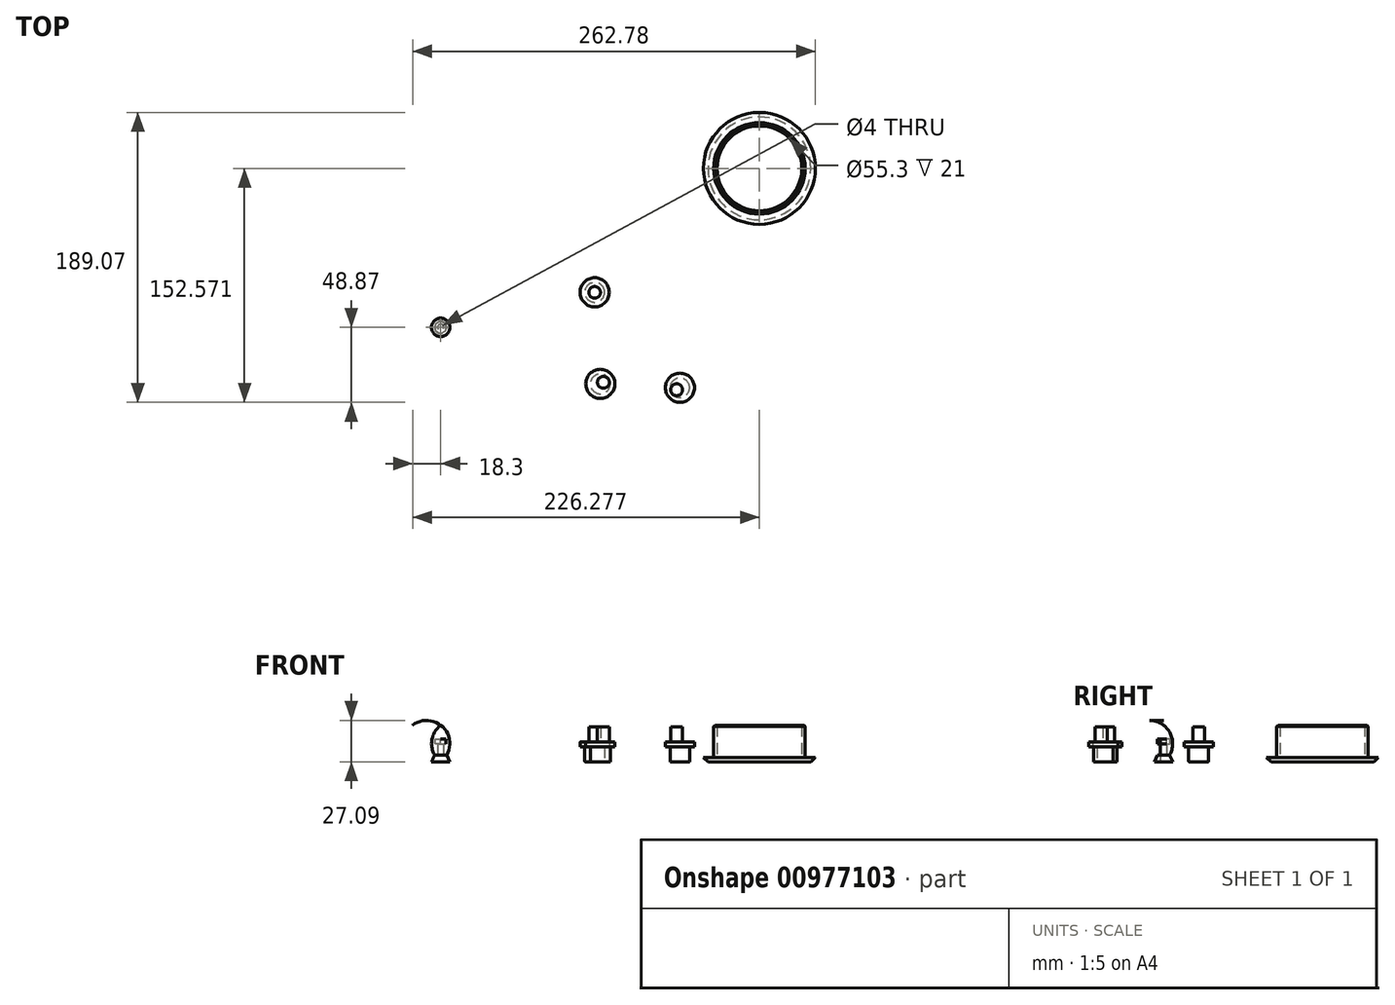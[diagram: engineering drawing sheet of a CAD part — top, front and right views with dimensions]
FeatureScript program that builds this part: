
annotation { "Feature Type Name" : "Feature", "Feature Type Description" : "" }
export const myFeature = defineFeature(function(context is Context, id is Id, definition is map)
    precondition{}
    {
        {
            var Q0;
            Q0=qCreatedBy(makeId("Front.planeOp"),FACE);
            var sketch = newSketch(context, id + "F0", { "sketchPlane" : qUnion([Q0])});
            skLineSegment(sketch, "E0.bottom", {"start": v(0, 0) * mm, "end": v(6, 0) * mm, "construction": true});
            skLineSegment(sketch, "E0.top", {"start": v(0, 24) * mm, "end": v(6, 24) * mm, "construction": true});
            skLineSegment(sketch, "E0.left", {"start": v(0, 0) * mm, "end": v(0, 24) * mm, "construction": true});
            skLineSegment(sketch, "E0.right", {"start": v(6, 0) * mm, "end": v(6, 24) * mm, "construction": true});
            skLineSegment(sketch, "E1", {"start": v(6, 4.5) * mm, "end": v(0, 4.5) * mm, "construction": true});
            skLineSegment(sketch, "E2", {"start": v(0, 24) * mm, "end": v(0, 28) * mm, "construction": true});
            skPoint(sketch, "E3", {"position": v(0.28, 24) * mm});
            skLineSegment(sketch, "E4", {"start": v(6, 14.25) * mm, "end": v(0, 14.25) * mm, "construction": true});
            skPoint(sketch, "E5", {"position": v(3, 24) * mm});
            skArc(sketch, "E6", {"start": v(3.94, 4.5) * mm, "mid": v(5.64, 15) * mm, "end": v(0, 24) * mm});
            skPoint(sketch, "E7", {"position": v(3.94, 4.5) * mm});
            skLineSegment(sketch, "E8", {"start": v(3.94, 4.5) * mm, "end": v(6, 0) * mm});
            skLineSegment(sketch, "E9", {"start": v(0, 0) * mm, "end": v(0, 24) * mm});
            skLineSegment(sketch, "E10", {"start": v(0, 0) * mm, "end": v(6, 0) * mm});
            skSolve(sketch);
        }
        {
            var Q0;
            Q0 = qSketchRegion(id + "F0", true);
            var Q1;
            Q1=sQuery(id+"F0.wireOp",EDGE,"E9");
            revolve(context, id + "F1", {"surfaceOperationType" : NewSurfaceOperationType.NEW, "entities" : qUnion([Q0]), "axis" : qUnion([Q1]), "revolveType" : RevolveType.FULL});
        }
        {
            var Q0;
            Q0=makeQuery(id+"F1.opRevolve","SWEPT_FACE",FACE,{"disambiguationData":[OSD([sQuery(id+"F0.wireOp",EDGE,"E10")])]});
            var sketch = newSketch(context, id + "F2", { "sketchPlane" : qUnion([Q0])});
            skCircle(sketch, "E11", {"center": v(0, 0) * mm, "radius": 2 * mm});
            skSolve(sketch);
        }
        {
            var Q0;
            Q0 = qSketchRegion(id + "F2", true);
            extrude(context, id + "F3", {"entities" : qUnion([Q0]), "operationType" : NewBodyOperationType.REMOVE, "oppositeDirection" : true, "depth" : 15 * mm, "offsetDistance" : 25 * mm});
        }
        {
            var Q0;
            Q0=makeQuery(id+"F3.boolean.opBoolean","COPY",FACE,{"derivedFrom":makeQuery(id+"F3.opExtrude","CAP_FACE",FACE,{"disambiguationData":[OSD([sQuery(id+"F2.wireOp",EDGE,"E11")])],"isStart":false})});
            var sketch = newSketch(context, id + "F4", { "sketchPlane" : qUnion([Q0])});
            skCircle(sketch, "E12.cCircle", {"center": v(0, 0) * mm, "radius": 4.1 * mm, "construction": true});
            skLineSegment(sketch, "E12.0", {"start": v(0, 4.1) * mm, "end": v(3.55, 2.05) * mm});
            skLineSegment(sketch, "E12.1", {"start": v(3.55, 2.05) * mm, "end": v(3.55, -2.05) * mm});
            skLineSegment(sketch, "E12.2", {"start": v(3.55, -2.05) * mm, "end": v(0, -4.1) * mm});
            skLineSegment(sketch, "E12.3", {"start": v(0, -4.1) * mm, "end": v(-3.55, -2.05) * mm});
            skLineSegment(sketch, "E12.4", {"start": v(-3.55, -2.05) * mm, "end": v(-3.55, 2.05) * mm});
            skLineSegment(sketch, "E12.5", {"start": v(-3.55, 2.05) * mm, "end": v(0, 4.1) * mm});
            skSolve(sketch);
        }
        {
            var Q0;
            Q0 = qSketchRegion(id + "F4", true);
            extrude(context, id + "F5", {"entities" : qUnion([Q0]), "operationType" : NewBodyOperationType.REMOVE, "depth" : 3.1 * mm, "offsetDistance" : 25 * mm});
        }
        {
            var Q0;
            Q0=qCreatedBy(makeId("Top.planeOp"),FACE);
            var sketch = newSketch(context, id + "F6", { "sketchPlane" : qUnion([Q0])});
            skCircle(sketch, "E13", {"center": v(100.5, 22.86) * mm, "radius": 6.45 * mm});
            skSolve(sketch);
        }
        {
            var Q0;
            Q0 = qSketchRegion(id + "F6", true);
            extrude(context, id + "F7", {"entities" : qUnion([Q0]), "depth" : 10 * mm, "offsetDistance" : 25 * mm});
        }
        {
            var Q0;
            Q0=makeQuery(id+"F7.opExtrude","CAP_FACE",FACE,{"disambiguationData":[OSD([sQuery(id+"F6.wireOp",EDGE,"E13")])],"isStart":false});
            var sketch = newSketch(context, id + "F8", { "sketchPlane" : qUnion([Q0])});
            skCircle(sketch, "E14", {"center": v(100.5, 22.86) * mm, "radius": 9.5 * mm});
            skSolve(sketch);
        }
        {
            var Q0;
            Q0=makeQuery(id+"F7.opExtrude","CAP_EDGE",EDGE,{"disambiguationData":[OSD([sQuery(id+"F6.wireOp",EDGE,"E13")])],"isStart":true});
            fillet(context, id + "F9", {"entities" : qUnion([Q0]), "tangentPropagation" : true, "radius" : 0.5 * mm, "defaultsChanged" : true, "vertexSettings" : [], "allowEdgeOverflow" : false});
        }
        {
            var Q0;
            Q0 = qSketchRegion(id + "F8", true);
            extrude(context, id + "F10", {"entities" : qUnion([Q0]), "operationType" : NewBodyOperationType.ADD, "depth" : 3 * mm, "offsetDistance" : 25 * mm});
        }
        {
            var Q0;
            Q0=makeQuery(id+"F10.opExtrude","CAP_FACE",FACE,{"disambiguationData":[OSD([sQuery(id+"F8.wireOp",EDGE,"E14")])],"isStart":false});
            var sketch = newSketch(context, id + "F11", { "sketchPlane" : qUnion([Q0])});
            skCircle(sketch, "E15", {"center": v(100.5, 22.86) * mm, "radius": 3.8 * mm});
            skSolve(sketch);
        }
        {
            var Q0;
            Q0 = qSketchRegion(id + "F11", true);
            extrude(context, id + "F12", {"entities" : qUnion([Q0]), "operationType" : NewBodyOperationType.ADD, "depth" : 10 * mm, "offsetDistance" : 25 * mm});
        }
        {
            var Q0;
            Q0=qCreatedBy(makeId("Top.planeOp"),FACE);
            var sketch = newSketch(context, id + "F13", { "sketchPlane" : qUnion([Q0])});
            skCircle(sketch, "E16", {"center": v(104.18, -36.85) * mm, "radius": 6.45 * mm});
            skSolve(sketch);
        }
        {
            var Q0;
            Q0 = qSketchRegion(id + "F13", true);
            extrude(context, id + "F14", {"entities" : qUnion([Q0]), "depth" : 10 * mm, "offsetDistance" : 25 * mm});
        }
        {
            var Q0;
            Q0=makeQuery(id+"F14.opExtrude","CAP_FACE",FACE,{"disambiguationData":[OSD([sQuery(id+"F13.wireOp",EDGE,"E16")])],"isStart":false});
            var sketch = newSketch(context, id + "F15", { "sketchPlane" : qUnion([Q0])});
            skCircle(sketch, "E17", {"center": v(104.18, -36.85) * mm, "radius": 9.5 * mm});
            skSolve(sketch);
        }
        {
            var Q0;
            Q0 = qSketchRegion(id + "F15", true);
            extrude(context, id + "F16", {"entities" : qUnion([Q0]), "operationType" : NewBodyOperationType.ADD, "depth" : 3 * mm, "offsetDistance" : 25 * mm});
        }
        {
            var Q0;
            Q0=makeQuery(id+"F16.opExtrude","CAP_FACE",FACE,{"disambiguationData":[OSD([sQuery(id+"F15.wireOp",EDGE,"E17")])],"isStart":false});
            var sketch = newSketch(context, id + "F17", { "sketchPlane" : qUnion([Q0])});
            skLineSegment(sketch, "E18", {"start": v(104.18, -36.85) * mm, "end": v(106.18, -36.85) * mm, "construction": true});
            skLineSegment(sketch, "E19", {"start": v(106.18, -36.85) * mm, "end": v(106.18, -35.85) * mm, "construction": true});
            skCircle(sketch, "E20", {"center": v(106.18, -35.85) * mm, "radius": 3.88 * mm});
            skSolve(sketch);
        }
        {
            var Q0;
            Q0=makeQuery(id+"F17.imprint","IMPRINT",FACE,{"disambiguationData":[TD([[makeQuery(id+"F17.imprint","IMPRINT",EDGE,{"derivedFrom":sQuery(id+"F17.wireOp",EDGE,"E20")}),1.0]])]});
            extrude(context, id + "F18", {"entities" : qUnion([Q0]), "operationType" : NewBodyOperationType.ADD, "depth" : 10 * mm, "offsetDistance" : 25 * mm});
        }
        {
            var Q0;
            Q0=qCreatedBy(makeId("Top.planeOp"),FACE);
            var sketch = newSketch(context, id + "F19", { "sketchPlane" : qUnion([Q0])});
            skCircle(sketch, "E21", {"center": v(156.11, -39.37) * mm, "radius": 6.35 * mm});
            skSolve(sketch);
        }
        {
            var Q0;
            Q0 = qSketchRegion(id + "F19", true);
            extrude(context, id + "F20", {"entities" : qUnion([Q0]), "depth" : 10 * mm, "offsetDistance" : 25 * mm});
        }
        {
            var Q0;
            Q0=makeQuery(id+"F20.opExtrude","CAP_FACE",FACE,{"disambiguationData":[OSD([sQuery(id+"F19.wireOp",EDGE,"E21")])],"isStart":false});
            var sketch = newSketch(context, id + "F21", { "sketchPlane" : qUnion([Q0])});
            skCircle(sketch, "E22", {"center": v(156.11, -39.37) * mm, "radius": 9.5 * mm});
            skSolve(sketch);
        }
        {
            var Q0;
            Q0 = qSketchRegion(id + "F21", true);
            extrude(context, id + "F22", {"entities" : qUnion([Q0]), "operationType" : NewBodyOperationType.ADD, "depth" : 3 * mm, "offsetDistance" : 25 * mm});
        }
        {
            var Q0;
            Q0=makeQuery(id+"F22.opExtrude","CAP_FACE",FACE,{"disambiguationData":[OSD([sQuery(id+"F21.wireOp",EDGE,"E22")])],"isStart":false});
            var sketch = newSketch(context, id + "F23", { "sketchPlane" : qUnion([Q0])});
            skCircle(sketch, "E23", {"center": v(156.11, -39.37) * mm, "radius": 6.4 * mm, "construction": true});
            skCircle(sketch, "E24", {"center": v(153.98, -40.7) * mm, "radius": 3.9 * mm});
            skSolve(sketch);
        }
        {
            var Q0;
            Q0 = qSketchRegion(id + "F23", true);
            extrude(context, id + "F24", {"entities" : qUnion([Q0]), "operationType" : NewBodyOperationType.ADD, "depth" : 10 * mm, "offsetDistance" : 25 * mm});
        }
        {
            var Q0;
            Q0=qCreatedBy(makeId("Top.planeOp"),FACE);
            var sketch = newSketch(context, id + "F25", { "sketchPlane" : qUnion([Q0])});
            skCircle(sketch, "E25", {"center": v(207.98, 103.7) * mm, "radius": 36.5 * mm});
            skSolve(sketch);
        }
        {
            var Q0;
            Q0 = qSketchRegion(id + "F25", true);
            extrude(context, id + "F26", {"entities" : qUnion([Q0]), "depth" : 3 * mm, "offsetDistance" : 25 * mm});
        }
        {
            var Q0;
            Q0=makeQuery(id+"F26.opExtrude","CAP_FACE",FACE,{"disambiguationData":[OSD([sQuery(id+"F25.wireOp",EDGE,"E25")])],"isStart":false});
            var sketch = newSketch(context, id + "F27", { "sketchPlane" : qUnion([Q0])});
            skCircle(sketch, "E26", {"center": v(207.98, 103.7) * mm, "radius": 29.85 * mm});
            skCircle(sketch, "E27.0", {"center": v(207.98, 103.7) * mm, "radius": 27.65 * mm});
            skSolve(sketch);
        }
        {
            var Q0;
            Q0 = qSketchRegion(id + "F27", true);
            extrude(context, id + "F28", {"entities" : qUnion([Q0]), "operationType" : NewBodyOperationType.ADD, "depth" : 21 * mm, "offsetDistance" : 25 * mm});
        }
        {
            var Q0;
            Q0=makeQuery(id+"F28.opExtrude","CAP_EDGE",EDGE,{"disambiguationData":[OSD([sQuery(id+"F27.wireOp",EDGE,"E26")])],"isStart":false});
            chamfer(context, id + "F29", {"entities" : qUnion([Q0]), "width" : 0.9 * mm, "tangentPropagation" : true});
        }
        {
            var Q0;
            Q0=makeQuery(id+"F26.opExtrude","CAP_EDGE",EDGE,{"disambiguationData":[OSD([sQuery(id+"F25.wireOp",EDGE,"E25")])],"isStart":true});
            chamfer(context, id + "F30", {"entities" : qUnion([Q0]), "width" : 3 * mm, "tangentPropagation" : true});
        }
    });
